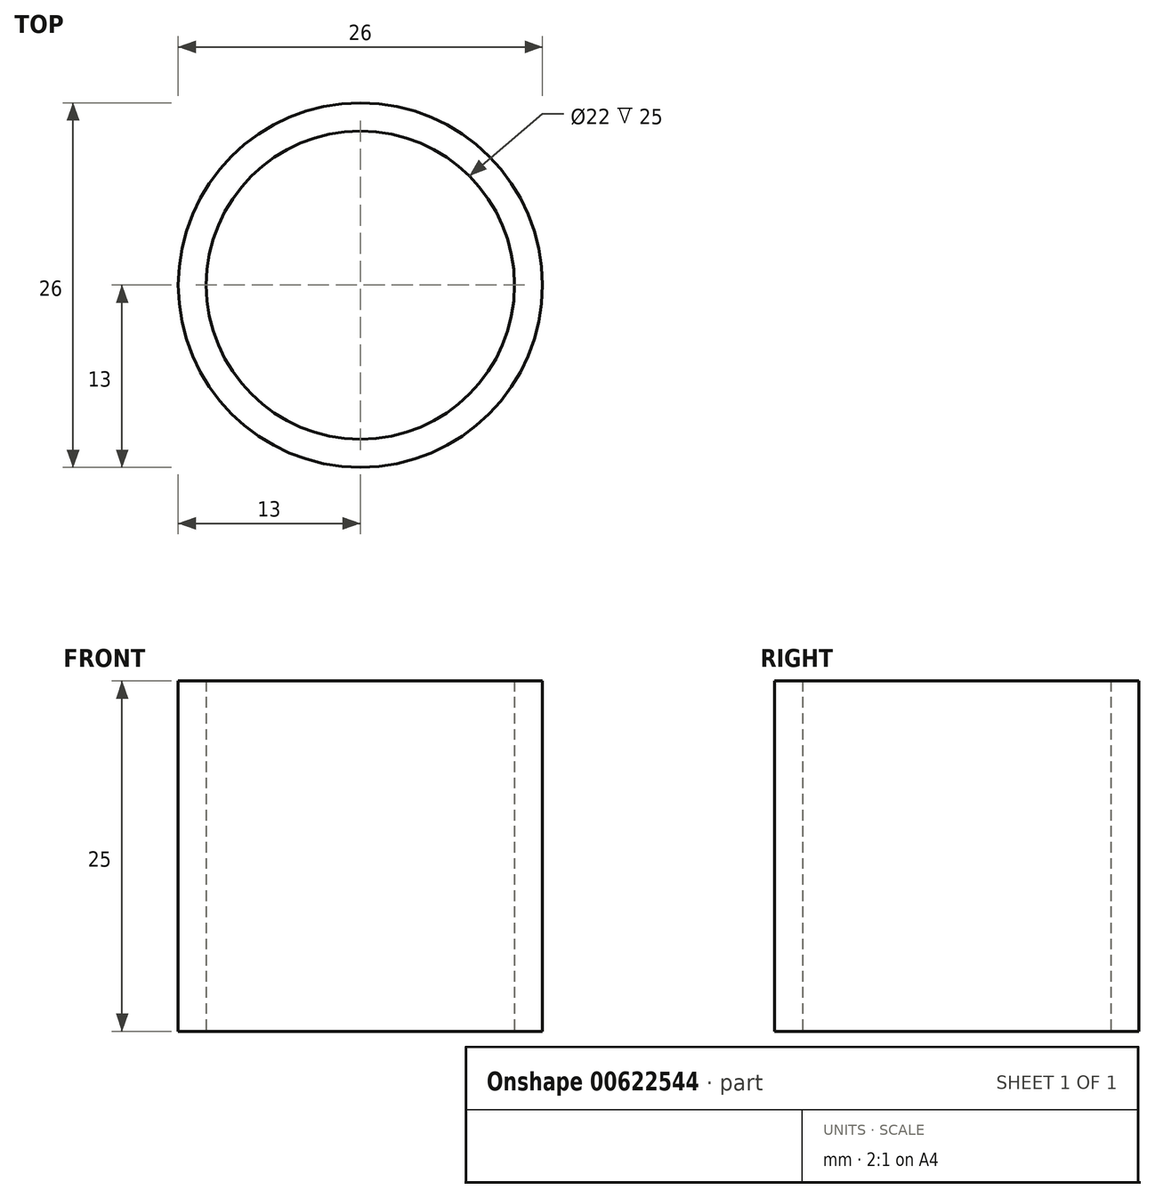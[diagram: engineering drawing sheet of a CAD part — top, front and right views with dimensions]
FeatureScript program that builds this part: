
annotation { "Feature Type Name" : "Feature", "Feature Type Description" : "" }
export const myFeature = defineFeature(function(context is Context, id is Id, definition is map)
    precondition{}
    {
        {
            var Q0;
            Q0=qCreatedBy(makeId("Top.planeOp"),FACE);
            var sketch = newSketch(context, id + "F0", { "sketchPlane" : qUnion([Q0])});
            skCircle(sketch, "E0", {"center": v(0, 0) * mm, "radius": 11 * mm});
            skCircle(sketch, "E1", {"center": v(0, 0) * mm, "radius": 13 * mm});
            skSolve(sketch);
        }
        {
            var Q0;
            Q0=makeQuery(id+"F0.imprint","IMPRINT",FACE,{"disambiguationData":[TD([[makeQuery(id+"F0.imprint","IMPRINT",EDGE,{"derivedFrom":sQuery(id+"F0.wireOp",EDGE,"E0")}),-1.0]])]});
            extrude(context, id + "F1", {"entities" : qUnion([Q0]), "depth" : 25 * mm, "offsetDistance" : 25 * mm});
        }
    });
